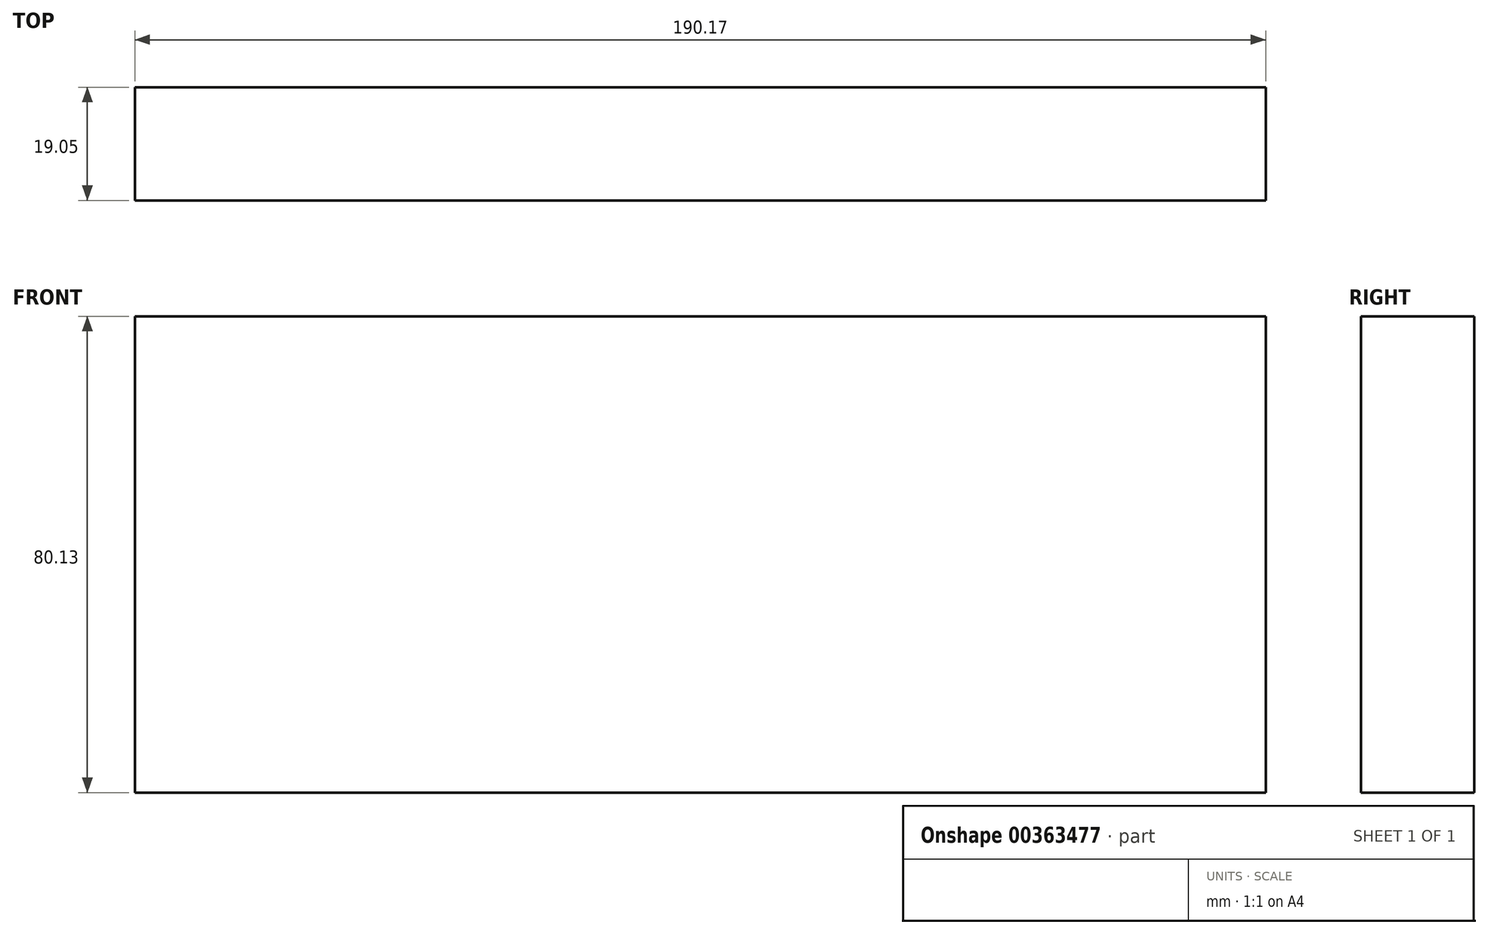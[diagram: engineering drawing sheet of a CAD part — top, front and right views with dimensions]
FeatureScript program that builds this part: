
annotation { "Feature Type Name" : "Feature", "Feature Type Description" : "" }
export const myFeature = defineFeature(function(context is Context, id is Id, definition is map)
    precondition{}
    {
        {
            var Q0;
            Q0=qCreatedBy(makeId("Front.planeOp"),FACE);
            var sketch = newSketch(context, id + "F0", { "sketchPlane" : qUnion([Q0])});
            skLineSegment(sketch, "E0.bottom", {"start": v(-48.19, 188.35) * mm, "end": v(141.98, 188.35) * mm});
            skLineSegment(sketch, "E0.top", {"start": v(-48.19, 108.22) * mm, "end": v(141.98, 108.22) * mm});
            skLineSegment(sketch, "E0.left", {"start": v(-48.19, 188.35) * mm, "end": v(-48.19, 108.22) * mm});
            skLineSegment(sketch, "E0.right", {"start": v(141.98, 188.35) * mm, "end": v(141.98, 108.22) * mm});
            skSolve(sketch);
        }
        {
            var Q0;
            Q0=makeQuery(id+"F0.imprint","IMPRINT",FACE,{"disambiguationData":[TD([[makeQuery(id+"F0.imprint","IMPRINT",EDGE,{"derivedFrom":sQuery(id+"F0.wireOp",EDGE,"E0.bottom")}),-1.0]])]});
            extrude(context, id + "F1", {"entities" : qUnion([Q0]), "depth" : 19.05 * mm});
        }
    });
